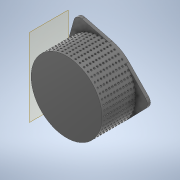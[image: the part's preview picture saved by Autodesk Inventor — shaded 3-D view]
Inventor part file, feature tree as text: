
AUTODESK INVENTOR PART (.ipt)
format: ipt  version: 2020 (Build 240168000, 168)  size: 1,464,832 bytes
history: native  units: in
note: dims shown in document units (in); Inventor stores cm internally (conversion verified against a paired STEP export)
features: sketch x6, extrude x4, projected_geometry x3, shell x1, plane x1, hole x1, pattern_circular x1
ambient origin geometry x8: Origin, YZ Plane, XZ Plane, XY Plane, X Axis, Y Axis, Z Axis, Center Point
bodies: Solid1 (feature_tree)
feature tree (17):
  extrude  "Extrusion1"  Depth=0.1181in
  shell  "Shell1"  Thickness=1.378in
  plane  "Work Plane1"
  hole  "Hole1"  [1 undecoded]
  pattern_circular  "Circular Pattern1"  Count=11  [1 undecoded]
  sketch  "Sketch3"  dims[d6=0.0984in d7=4.3307in d9=0.1181in d10=0.3937in d12=0.3937in]
  extrude  "Extrusion2"  Depth=9.8425in TaperAngle=360.0deg
  extrude  "Extrusion3"  TaperAngle=120.0deg  [1 undecoded]
  extrude  "Extrusion4"  Depth=1.5748in
  sketch  "Sketch1"  dims[d0=2.5197in d1=0.1181in d2=1.378in d3=0.0in]
  sketch  "Sketch2"  dims[d4=0.0591in d5=0.0591in]
  projected_geometry  "Projected Loop1"
  sketch  "Sketch4"  dims[d14=0.0591in d15=0.2362in d16=0.1575in d17=0.0787in d18=90.0deg d19=0.315in d20=0.8108in d21=9.8425in d22=360.0deg]
  projected_geometry  "Projected Loop2"
  sketch  "Sketch5"  dims[d24=120.0deg d25=120.0deg]
  projected_geometry  "Projected Loop3"
  sketch  "Sketch6"  dims[d26=0.378in d27=1.5748in d28=1.5748in d29=1.5748in d30=0.378in d31=0.378in d32=0.0591in d33=0.0591in d34=0.0591in d35=0.1181in d36=0.0in d37=0.1181in d38=0.0in d39=0.378in d40=1.5748in d41=1.1811in d43=360.0deg d45=0.06in d46=0.0in]
note: 3 required parameter values undecoded (feature->parameter linkage not recoverable at this tier; creation-order binding heuristic only, values carry confidence <= 0.55)
